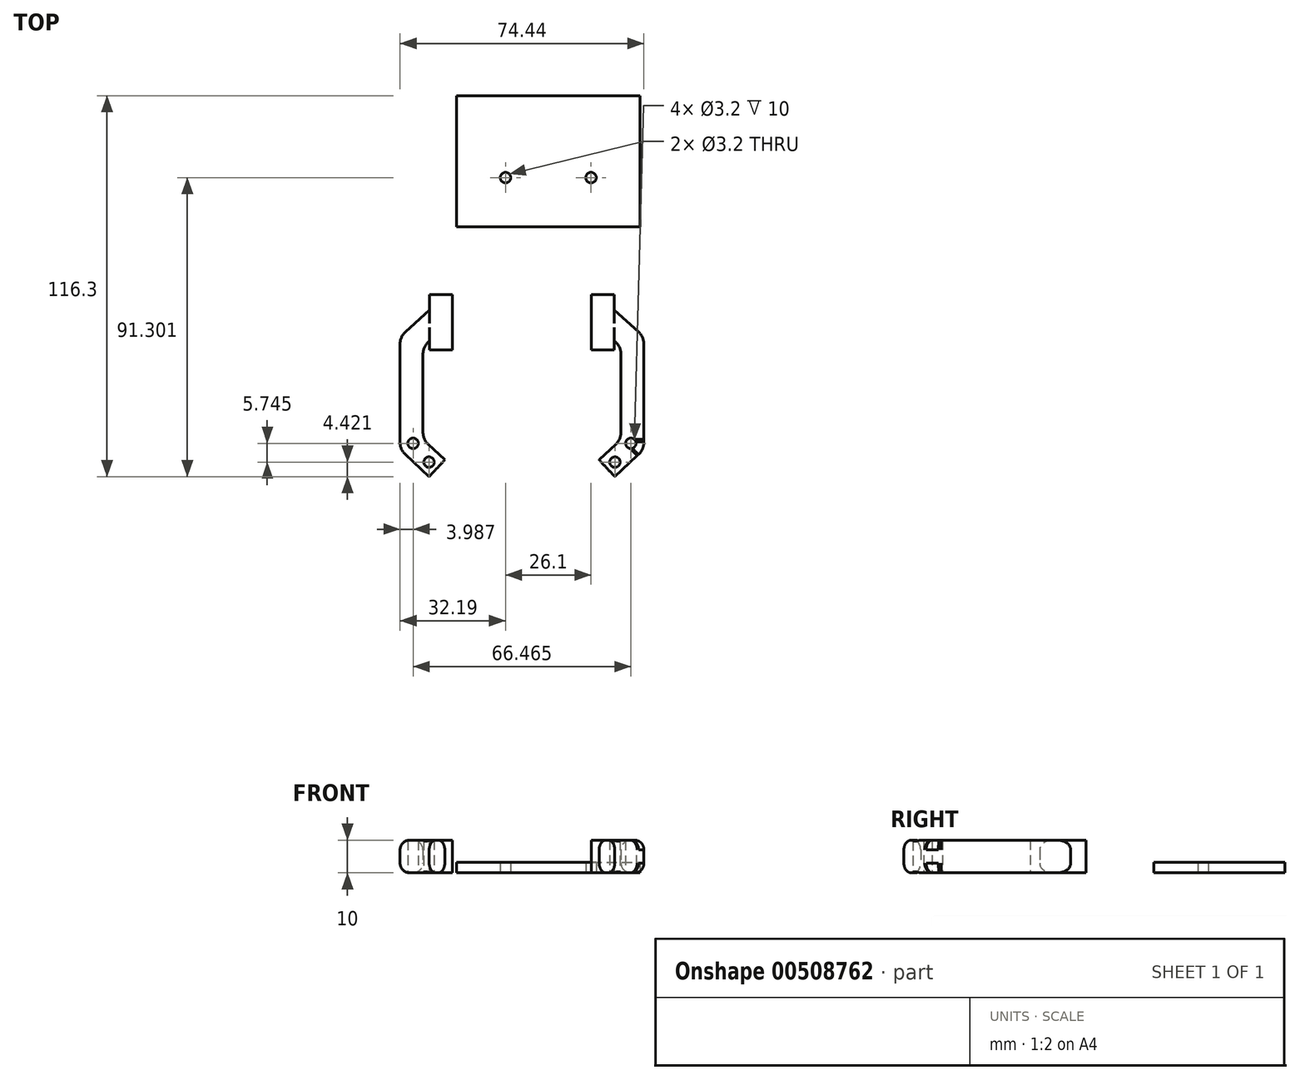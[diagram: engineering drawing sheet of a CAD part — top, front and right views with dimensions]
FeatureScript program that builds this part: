
annotation { "Feature Type Name" : "Feature", "Feature Type Description" : "" }
export const myFeature = defineFeature(function(context is Context, id is Id, definition is map)
    precondition{}
    {
        {
            var Q0;
            Q0=qCreatedBy(makeId("Top.planeOp"),FACE);
            var sketch = newSketch(context, id + "F0", { "sketchPlane" : qUnion([Q0])});
            skLineSegment(sketch, "E0.bottom", {"start": v(-39.21, 32.42) * mm, "end": v(16.89, 32.42) * mm});
            skLineSegment(sketch, "E0.top", {"start": v(-39.21, -7.58) * mm, "end": v(16.89, -7.58) * mm});
            skLineSegment(sketch, "E0.left", {"start": v(-39.21, 32.42) * mm, "end": v(-39.21, -7.58) * mm});
            skLineSegment(sketch, "E0.right", {"start": v(16.89, 32.42) * mm, "end": v(16.89, -7.58) * mm});
            skCircle(sketch, "E1", {"center": v(-24.21, 7.42) * mm, "radius": 1.6 * mm});
            skCircle(sketch, "E2", {"center": v(1.89, 7.42) * mm, "radius": 1.6 * mm});
            skSolve(sketch);
        }
        {
            var Q0;
            Q0=makeQuery(id+"F0.imprint","IMPRINT",FACE,{"disambiguationData":[TD([[makeQuery(id+"F0.imprint","IMPRINT",EDGE,{"derivedFrom":sQuery(id+"F0.wireOp",EDGE,"E0.bottom")}),-1.0]])]});
            extrude(context, id + "F1", {"entities" : qUnion([Q0]), "depth" : 3.2 * mm});
        }
        {
            var Q0;
            Q0=qCreatedBy(makeId("Top.planeOp"),FACE);
            var sketch = newSketch(context, id + "F2", { "sketchPlane" : qUnion([Q0])});
            skLineSegment(sketch, "E3", {"start": v(-56.4, -73.4) * mm, "end": v(-56.4, -43.4) * mm});
            skLineSegment(sketch, "E4", {"start": v(-54.78, -39.7) * mm, "end": v(-47.4, -32.96) * mm});
            skLineSegment(sketch, "E5", {"start": v(-54.81, -77.05) * mm, "end": v(-47.5, -83.88) * mm});
            skLineSegment(sketch, "E6.0", {"start": v(-47.78, -42.79) * mm, "end": v(-47.4, -42.45) * mm});
            skLineSegment(sketch, "E6.1", {"start": v(-49.4, -70.36) * mm, "end": v(-49.4, -46.48) * mm});
            skLineSegment(sketch, "E6.2", {"start": v(-47.81, -74) * mm, "end": v(-42.73, -78.76) * mm});
            skLineSegment(sketch, "E7.bottom", {"start": v(-47.4, -28.26) * mm, "end": v(-40.4, -28.26) * mm});
            skLineSegment(sketch, "E7.top", {"start": v(-47.4, -45.26) * mm, "end": v(-40.4, -45.26) * mm});
            skLineSegment(sketch, "E7.left", {"start": v(-47.4, -28.26) * mm, "end": v(-47.4, -45.26) * mm});
            skLineSegment(sketch, "E7.right", {"start": v(-40.4, -28.26) * mm, "end": v(-40.4, -45.26) * mm});
            skLineSegment(sketch, "E8", {"start": v(-42.73, -78.76) * mm, "end": v(-47.5, -83.88) * mm});
            skLineSegment(sketch, "E9", {"start": v(-19.18, -23.93) * mm, "end": v(-19.18, -82.78) * mm, "construction": true});
            skLineSegment(sketch, "E10.MirrorCS", {"start": v(9.04, -45.26) * mm, "end": v(2.04, -45.26) * mm});
            skLineSegment(sketch, "E11.MirrorCS", {"start": v(9.04, -28.26) * mm, "end": v(2.04, -28.26) * mm});
            skLineSegment(sketch, "E12.MirrorCS", {"start": v(2.04, -28.26) * mm, "end": v(2.04, -45.26) * mm});
            skLineSegment(sketch, "E13.MirrorCS", {"start": v(9.41, -42.79) * mm, "end": v(9.04, -42.45) * mm});
            skLineSegment(sketch, "E14.MirrorCS", {"start": v(4.37, -78.76) * mm, "end": v(9.15, -83.88) * mm});
            skLineSegment(sketch, "E15.MirrorCS", {"start": v(9.45, -74) * mm, "end": v(4.37, -78.76) * mm});
            skLineSegment(sketch, "E16.MirrorCS", {"start": v(11.04, -70.36) * mm, "end": v(11.04, -46.48) * mm});
            skLineSegment(sketch, "E17.MirrorCS", {"start": v(18.04, -73.4) * mm, "end": v(18.04, -43.4) * mm});
            skLineSegment(sketch, "E18.MirrorCS", {"start": v(9.04, -28.26) * mm, "end": v(9.04, -45.26) * mm});
            skLineSegment(sketch, "E19.MirrorCS", {"start": v(16.41, -39.7) * mm, "end": v(9.04, -32.96) * mm});
            skLineSegment(sketch, "E20.MirrorCS", {"start": v(16.45, -77.05) * mm, "end": v(9.15, -83.88) * mm});
            skCircle(sketch, "E21", {"center": v(-47.56, -79.46) * mm, "radius": 1.6 * mm});
            skCircle(sketch, "E22", {"center": v(-52.41, -73.71) * mm, "radius": 1.6 * mm});
            skCircle(sketch, "E23.MirrorC", {"center": v(9.2, -79.46) * mm, "radius": 1.6 * mm});
            skCircle(sketch, "E24.MirrorC", {"center": v(14.05, -73.71) * mm, "radius": 1.6 * mm});
            skPoint(sketch, "E25.visualSharp", {"position": v(-49.4, -44.28) * mm});
            skArc(sketch, "E25.filletArc", {"start": v(-47.78, -42.79) * mm, "mid": v(-48.98, -44.46) * mm, "end": v(-49.4, -46.48) * mm});
            skPoint(sketch, "E26.visualSharp", {"position": v(-56.4, -41.2) * mm});
            skArc(sketch, "E26.filletArc", {"start": v(-54.78, -39.7) * mm, "mid": v(-55.98, -41.38) * mm, "end": v(-56.4, -43.4) * mm});
            skPoint(sketch, "E27.visualSharp", {"position": v(-49.4, -72.53) * mm});
            skArc(sketch, "E27.filletArc", {"start": v(-49.4, -70.36) * mm, "mid": v(-48.99, -72.35) * mm, "end": v(-47.81, -74) * mm});
            skPoint(sketch, "E28.visualSharp", {"position": v(-56.4, -75.57) * mm});
            skArc(sketch, "E28.filletArc", {"start": v(-56.4, -73.4) * mm, "mid": v(-55.99, -75.39) * mm, "end": v(-54.81, -77.05) * mm});
            skArc(sketch, "E29.MirrorCS", {"start": v(18.04, -73.4) * mm, "mid": v(17.63, -75.39) * mm, "end": v(16.45, -77.05) * mm});
            skArc(sketch, "E30.MirrorCS", {"start": v(11.04, -70.36) * mm, "mid": v(10.63, -72.35) * mm, "end": v(9.45, -74) * mm});
            skArc(sketch, "E31.MirrorCS", {"start": v(16.41, -39.7) * mm, "mid": v(17.62, -41.38) * mm, "end": v(18.04, -43.4) * mm});
            skArc(sketch, "E32.MirrorCS", {"start": v(9.41, -42.79) * mm, "mid": v(10.62, -44.46) * mm, "end": v(11.04, -46.48) * mm});
            skPoint(sketch, "E33.orphan", {"position": v(11.04, -72.53) * mm});
            skPoint(sketch, "E34.orphan", {"position": v(18.04, -75.57) * mm});
            skPoint(sketch, "E35.orphan", {"position": v(11.04, -44.28) * mm});
            skPoint(sketch, "E36.orphan", {"position": v(18.04, -41.2) * mm});
            skSolve(sketch);
        }
        {
            var Q0;
            Q0=qSketchRegion(id+"F2",true);
            extrude(context, id + "F3", {"entities" : qUnion([Q0]), "depth" : 10 * mm});
        }
        {
            var Q0;
            Q0=makeQuery(id+"F3.opExtrude","CAP_EDGE",EDGE,{"disambiguationData":[OSD([sQuery(id+"F2.wireOp",EDGE,"E6.1")])],"isStart":false});
            var Q1;
            Q1=makeQuery(id+"F3.opExtrude","CAP_EDGE",EDGE,{"disambiguationData":[OSD([sQuery(id+"F2.wireOp",EDGE,"E16.MirrorCS")])],"isStart":false});
            var Q2;
            Q2=makeQuery(id+"F3.opExtrude","CAP_EDGE",EDGE,{"disambiguationData":[OSD([sQuery(id+"F2.wireOp",EDGE,"E17.MirrorCS")])],"isStart":false});
            var Q3;
            Q3=makeQuery(id+"F3.opExtrude","CAP_EDGE",EDGE,{"disambiguationData":[OSD([sQuery(id+"F2.wireOp",EDGE,"E3")])],"isStart":false});
            var Q4;
            Q4=makeQuery(id+"F3.opExtrude","CAP_EDGE",EDGE,{"disambiguationData":[OSD([sQuery(id+"F2.wireOp",EDGE,"E3")])],"isStart":true});
            var Q5;
            Q5=makeQuery(id+"F3.opExtrude","CAP_EDGE",EDGE,{"disambiguationData":[OSD([sQuery(id+"F2.wireOp",EDGE,"E6.1")])],"isStart":true});
            var Q6;
            Q6=makeQuery(id+"F3.opExtrude","CAP_EDGE",EDGE,{"disambiguationData":[OSD([sQuery(id+"F2.wireOp",EDGE,"E16.MirrorCS")])],"isStart":true});
            var Q7;
            Q7=makeQuery(id+"F3.opExtrude","CAP_EDGE",EDGE,{"disambiguationData":[OSD([sQuery(id+"F2.wireOp",EDGE,"E17.MirrorCS")])],"isStart":true});
            fillet(context, id + "F4", {"entities" : qUnion([Q0, Q1, Q2, Q3, Q4, Q5, Q6, Q7]), "radius" : 3 * mm, "tangentPropagation" : true, "allowEdgeOverflow" : false});
        }
    });
